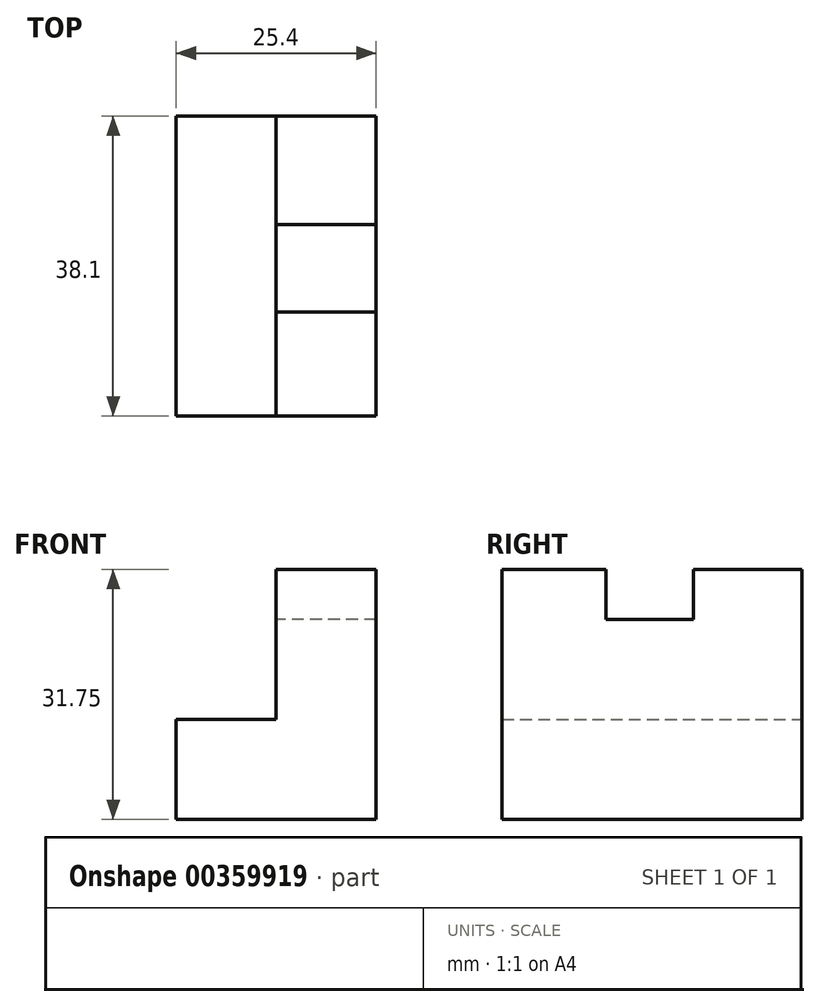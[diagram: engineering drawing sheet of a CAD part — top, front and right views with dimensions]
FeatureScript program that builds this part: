
annotation { "Feature Type Name" : "Feature", "Feature Type Description" : "" }
export const myFeature = defineFeature(function(context is Context, id is Id, definition is map)
    precondition{}
    {
        {
            var Q0;
            Q0=qCreatedBy(makeId("Front.planeOp"),FACE);
            var sketch = newSketch(context, id + "F0", { "sketchPlane" : qUnion([Q0])});
            skLineSegment(sketch, "E0", {"start": v(0, 0) * mm, "end": v(-25.4, 0) * mm});
            skLineSegment(sketch, "E1", {"start": v(-25.4, 0) * mm, "end": v(-25.4, 12.7) * mm});
            skLineSegment(sketch, "E2", {"start": v(-25.4, 12.7) * mm, "end": v(-12.7, 12.7) * mm});
            skLineSegment(sketch, "E3", {"start": v(-12.7, 12.7) * mm, "end": v(-12.7, 12.7) * mm});
            skLineSegment(sketch, "E4", {"start": v(-12.7, 12.7) * mm, "end": v(-12.7, 31.75) * mm});
            skLineSegment(sketch, "E5", {"start": v(-12.7, 31.75) * mm, "end": v(0, 31.75) * mm});
            skLineSegment(sketch, "E6", {"start": v(0, 31.75) * mm, "end": v(0, 0) * mm});
            skLineSegment(sketch, "E7", {"start": v(-1.06, 0.44) * mm, "end": v(0, 0) * mm});
            skSolve(sketch);
        }
        {
            var Q0;
            Q0 = qSketchRegion(id + "F0", true);
            extrude(context, id + "F1", {"entities" : qUnion([Q0]), "depth" : 38.1 * mm});
        }
        {
            var Q0;
            Q0=makeQuery(id+"F1.opExtrude","SWEPT_FACE",FACE,{"disambiguationData":[OSD([sQuery(id+"F0.wireOp",EDGE,"E5")])]});
            var sketch = newSketch(context, id + "F2", { "sketchPlane" : qUnion([Q0])});
            skLineSegment(sketch, "E8", {"start": v(-12.7, -13.77) * mm, "end": v(0, -13.77) * mm});
            skLineSegment(sketch, "E9", {"start": v(0, -13.77) * mm, "end": v(0, -24.92) * mm});
            skLineSegment(sketch, "E10", {"start": v(0, -24.92) * mm, "end": v(-12.7, -24.92) * mm});
            skLineSegment(sketch, "E11", {"start": v(-10.83, -23.68) * mm, "end": v(-12.7, -24.92) * mm});
            skLineSegment(sketch, "E12", {"start": v(-12.7, -24.92) * mm, "end": v(-12.7, -13.77) * mm});
            skSolve(sketch);
        }
        {
            var Q0;
            Q0 = qSketchRegion(id + "F2", true);
            extrude(context, id + "F3", {"entities" : qUnion([Q0]), "operationType" : NewBodyOperationType.REMOVE, "oppositeDirection" : true, "depth" : 6.35 * mm});
        }
    });
